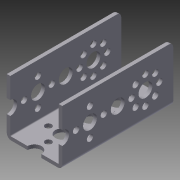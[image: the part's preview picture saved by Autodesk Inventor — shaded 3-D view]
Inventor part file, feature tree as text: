
AUTODESK INVENTOR PART (.ipt)
format: ipt  version: 2014 SP2 (Build 180246200, 246)  size: 306,688 bytes
history: native  units: in
note: dims shown in document units (in); Inventor stores cm internally (conversion verified against a paired STEP export)
features: other x1, extrude x1, imported_body x1, sketch x1
ambient origin geometry x8: Origin, YZ Plane, XZ Plane, XY Plane, X Axis, Y Axis, Z Axis, Center Point
bodies: Solid1 (feature_tree)
feature tree (4):
  other  "96mm Channel.sat1"
  extrude  "Extrusion1"  [1 undecoded]
  imported_body  "Base1"
  sketch  "Sketch1"  dims[d0=3.937in d1=0.0in]
note: 1 required parameter value undecoded (feature->parameter linkage not recoverable at this tier; creation-order binding heuristic only, values carry confidence <= 0.55)
